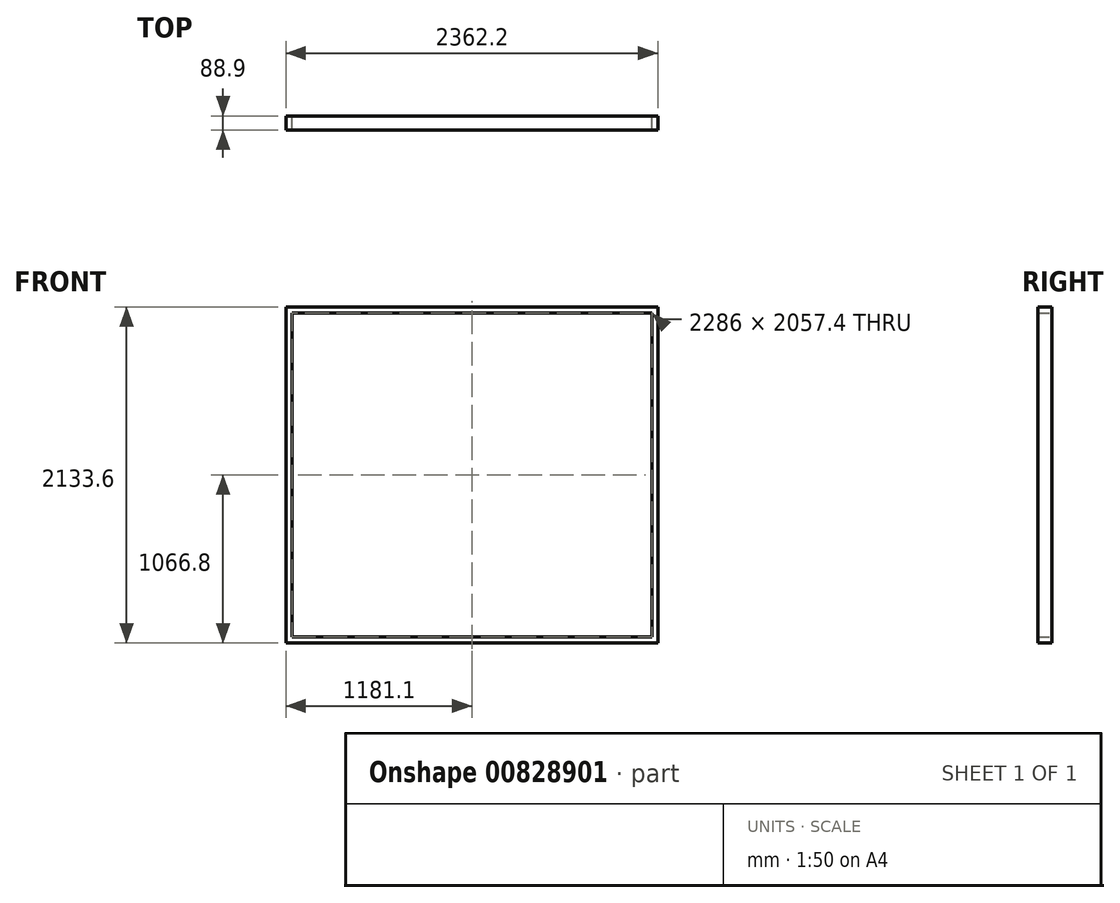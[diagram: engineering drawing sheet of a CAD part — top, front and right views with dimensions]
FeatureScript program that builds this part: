
annotation { "Feature Type Name" : "Feature", "Feature Type Description" : "" }
export const myFeature = defineFeature(function(context is Context, id is Id, definition is map)
    precondition{}
    {
        {
            var Q0;
            Q0=qCreatedBy(makeId("Front.planeOp"),FACE);
            var sketch = newSketch(context, id + "F0", { "sketchPlane" : qUnion([Q0])});
            skLineSegment(sketch, "E0.bottom", {"start": v(0, 0) * mm, "end": v(2362.2, 0) * mm});
            skLineSegment(sketch, "E0.top", {"start": v(0, 38.1) * mm, "end": v(2362.2, 38.1) * mm});
            skLineSegment(sketch, "E0.left", {"start": v(0, 0) * mm, "end": v(0, 38.1) * mm});
            skLineSegment(sketch, "E0.right", {"start": v(2362.2, 0) * mm, "end": v(2362.2, 38.1) * mm});
            skLineSegment(sketch, "E1.bottom", {"start": v(2362.2, 38.1) * mm, "end": v(2324.1, 38.1) * mm});
            skLineSegment(sketch, "E1.top", {"start": v(2362.2, 2095.5) * mm, "end": v(2324.1, 2095.5) * mm});
            skLineSegment(sketch, "E1.left", {"start": v(2362.2, 38.1) * mm, "end": v(2362.2, 2095.5) * mm});
            skLineSegment(sketch, "E1.right", {"start": v(2324.1, 38.1) * mm, "end": v(2324.1, 2095.5) * mm});
            skLineSegment(sketch, "E2.bottom", {"start": v(0, 38.1) * mm, "end": v(38.1, 38.1) * mm});
            skLineSegment(sketch, "E2.top", {"start": v(0, 2095.5) * mm, "end": v(38.1, 2095.5) * mm});
            skLineSegment(sketch, "E2.left", {"start": v(0, 38.1) * mm, "end": v(0, 2095.5) * mm});
            skLineSegment(sketch, "E2.right", {"start": v(38.1, 38.1) * mm, "end": v(38.1, 2095.5) * mm});
            skLineSegment(sketch, "E3.bottom", {"start": v(38.1, 38.1) * mm, "end": v(406.4, 38.1) * mm, "construction": true});
            skLineSegment(sketch, "E3.top", {"start": v(38.1, 38.1) * mm, "end": v(406.4, 38.1) * mm, "construction": true});
            skLineSegment(sketch, "E3.left", {"start": v(38.1, 38.1) * mm, "end": v(38.1, 38.1) * mm});
            skLineSegment(sketch, "E3.right", {"start": v(406.4, 38.1) * mm, "end": v(406.4, 38.1) * mm});
            skLineSegment(sketch, "E4.bottom", {"start": v(406.4, 38.1) * mm, "end": v(444.5, 38.1) * mm});
            skLineSegment(sketch, "E4.top", {"start": v(406.4, 2095.5) * mm, "end": v(444.5, 2095.5) * mm});
            skLineSegment(sketch, "E4.left", {"start": v(406.4, 38.1) * mm, "end": v(406.4, 2095.5) * mm});
            skLineSegment(sketch, "E4.right", {"start": v(444.5, 38.1) * mm, "end": v(444.5, 2095.5) * mm});
            skLineSegment(sketch, "E5", {"start": v(444.5, 38.1) * mm, "end": v(812.8, 38.1) * mm, "construction": true});
            skLineSegment(sketch, "E6.bottom", {"start": v(812.8, 38.1) * mm, "end": v(850.9, 38.1) * mm});
            skLineSegment(sketch, "E6.top", {"start": v(812.8, 2095.5) * mm, "end": v(850.9, 2095.5) * mm});
            skLineSegment(sketch, "E6.left", {"start": v(812.8, 38.1) * mm, "end": v(812.8, 2095.5) * mm});
            skLineSegment(sketch, "E6.right", {"start": v(850.9, 38.1) * mm, "end": v(850.9, 2095.5) * mm});
            skLineSegment(sketch, "E7", {"start": v(850.9, 38.1) * mm, "end": v(1219.2, 38.1) * mm, "construction": true});
            skLineSegment(sketch, "E8.bottom", {"start": v(1219.2, 38.1) * mm, "end": v(1257.3, 38.1) * mm});
            skLineSegment(sketch, "E8.top", {"start": v(1219.2, 2095.5) * mm, "end": v(1257.3, 2095.5) * mm});
            skLineSegment(sketch, "E8.left", {"start": v(1219.2, 38.1) * mm, "end": v(1219.2, 2095.5) * mm});
            skLineSegment(sketch, "E8.right", {"start": v(1257.3, 38.1) * mm, "end": v(1257.3, 2095.5) * mm});
            skLineSegment(sketch, "E9", {"start": v(1257.3, 38.1) * mm, "end": v(1625.6, 38.1) * mm, "construction": true});
            skLineSegment(sketch, "E10.bottom", {"start": v(1625.6, 38.1) * mm, "end": v(1663.7, 38.1) * mm});
            skLineSegment(sketch, "E10.top", {"start": v(1625.6, 2095.5) * mm, "end": v(1663.7, 2095.5) * mm});
            skLineSegment(sketch, "E10.left", {"start": v(1625.6, 38.1) * mm, "end": v(1625.6, 2095.5) * mm});
            skLineSegment(sketch, "E10.right", {"start": v(1663.7, 38.1) * mm, "end": v(1663.7, 2095.5) * mm});
            skLineSegment(sketch, "E11", {"start": v(1663.7, 38.1) * mm, "end": v(2032, 38.1) * mm, "construction": true});
            skLineSegment(sketch, "E12.bottom", {"start": v(2032, 38.1) * mm, "end": v(2070.1, 38.1) * mm});
            skLineSegment(sketch, "E12.top", {"start": v(2032, 2095.5) * mm, "end": v(2070.1, 2095.5) * mm});
            skLineSegment(sketch, "E12.left", {"start": v(2032, 38.1) * mm, "end": v(2032, 2095.5) * mm});
            skLineSegment(sketch, "E12.right", {"start": v(2070.1, 38.1) * mm, "end": v(2070.1, 2095.5) * mm});
            skLineSegment(sketch, "E13.bottom", {"start": v(0, 2095.5) * mm, "end": v(2362.2, 2095.5) * mm});
            skLineSegment(sketch, "E13.top", {"start": v(0, 2133.6) * mm, "end": v(2362.2, 2133.6) * mm});
            skLineSegment(sketch, "E13.left", {"start": v(0, 2095.5) * mm, "end": v(0, 2133.6) * mm});
            skLineSegment(sketch, "E13.right", {"start": v(2362.2, 2095.5) * mm, "end": v(2362.2, 2133.6) * mm});
            skSolve(sketch);
        }
        {
            var Q0;
            Q0 = qSketchRegion(id + "F0", true);
            var Q1;
            Q1=makeQuery(id+"F0.imprint","IMPRINT",FACE,{"disambiguationData":[TD([[makeQuery(id+"F0.imprint","IMPRINT",EDGE,{"derivedFrom":sQuery(id+"F0.wireOp",EDGE,"E4.bottom")}),1.0]])]});
            var Q2;
            Q2=makeQuery(id+"F0.imprint","IMPRINT",FACE,{"disambiguationData":[TD([[makeQuery(id+"F0.imprint","IMPRINT",EDGE,{"derivedFrom":sQuery(id+"F0.wireOp",EDGE,"E6.bottom")}),1.0]])]});
            var Q3;
            Q3=makeQuery(id+"F0.imprint","IMPRINT",FACE,{"disambiguationData":[TD([[makeQuery(id+"F0.imprint","IMPRINT",EDGE,{"derivedFrom":sQuery(id+"F0.wireOp",EDGE,"E8.bottom")}),1.0]])]});
            var Q4;
            Q4=makeQuery(id+"F0.imprint","IMPRINT",FACE,{"disambiguationData":[TD([[makeQuery(id+"F0.imprint","IMPRINT",EDGE,{"derivedFrom":sQuery(id+"F0.wireOp",EDGE,"E10.bottom")}),1.0]])]});
            var Q5;
            Q5=makeQuery(id+"F0.imprint","IMPRINT",FACE,{"disambiguationData":[TD([[makeQuery(id+"F0.imprint","IMPRINT",EDGE,{"derivedFrom":sQuery(id+"F0.wireOp",EDGE,"E12.bottom")}),1.0]])]});
            extrude(context, id + "F1", {"entities" : qUnion([Q0, Q1, Q2, Q3, Q4, Q5]), "depth" : 88.9 * mm, "offsetDistance" : 25.4 * mm});
        }
    });
